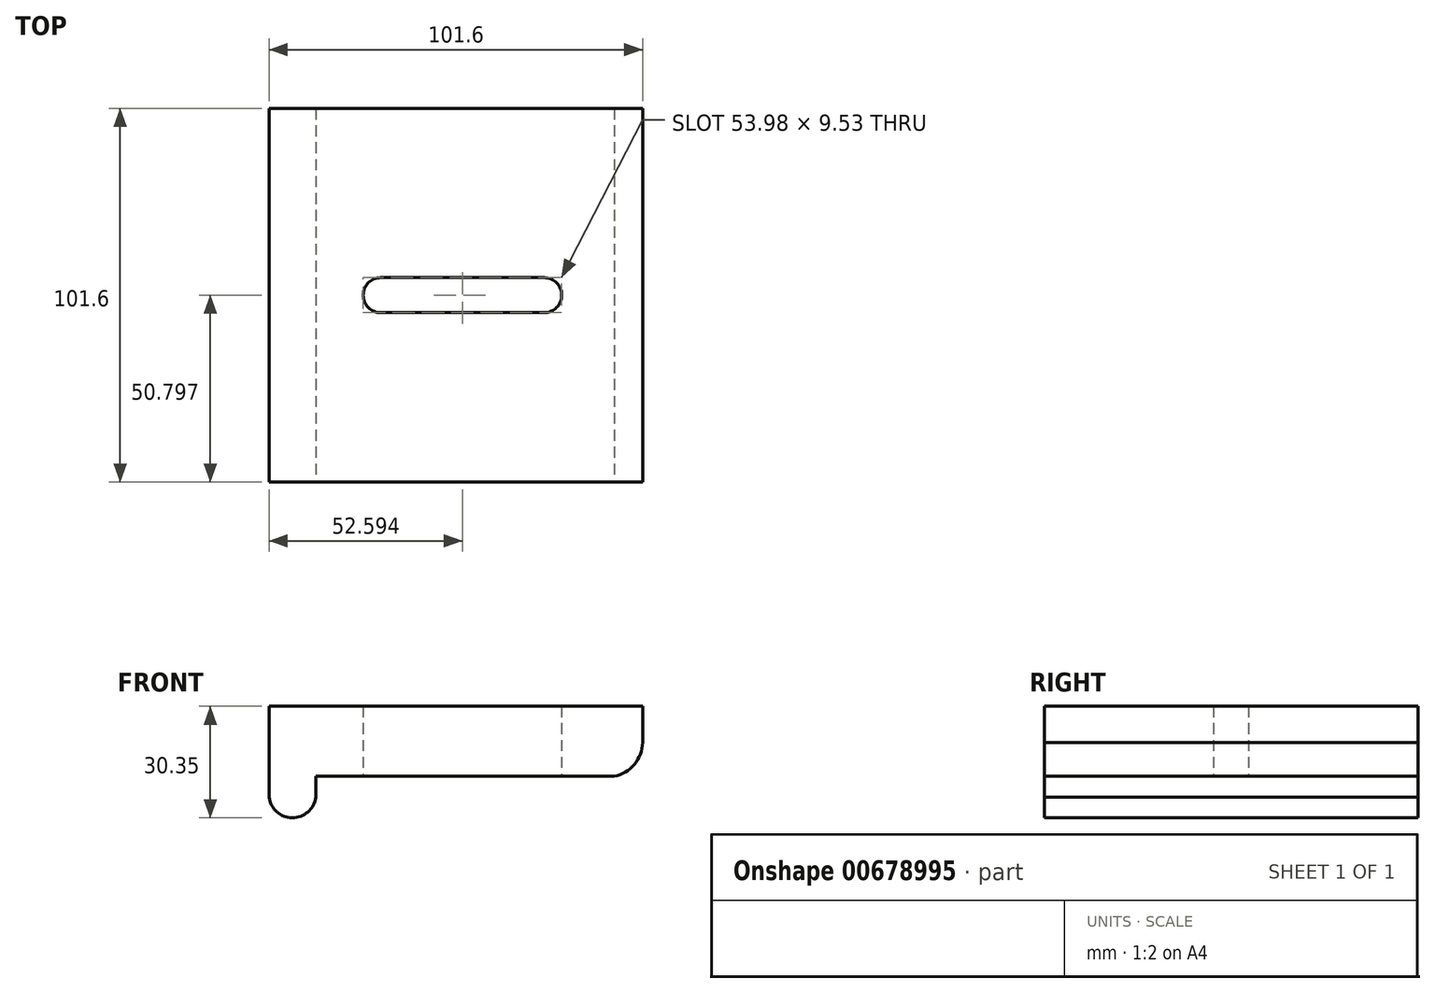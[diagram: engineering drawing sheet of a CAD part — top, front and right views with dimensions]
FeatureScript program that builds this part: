
annotation { "Feature Type Name" : "Feature", "Feature Type Description" : "" }
export const myFeature = defineFeature(function(context is Context, id is Id, definition is map)
    precondition{}
    {
        {
            var Q0;
            Q0=qCreatedBy(makeId("Top.planeOp"),FACE);
            var sketch = newSketch(context, id + "F0", { "sketchPlane" : qUnion([Q0])});
            skLineSegment(sketch, "E0", {"start": v(-101.34, 65.1) * mm, "end": v(-101.34, -36.5) * mm});
            skLineSegment(sketch, "E1", {"start": v(-101.34, -36.5) * mm, "end": v(0.26, -36.5) * mm});
            skLineSegment(sketch, "E2", {"start": v(0.26, -36.5) * mm, "end": v(0.26, 65.1) * mm});
            skLineSegment(sketch, "E3", {"start": v(0.26, 65.1) * mm, "end": v(-101.34, 65.1) * mm});
            skLineSegment(sketch, "E4", {"start": v(-70.97, 19.06) * mm, "end": v(-26.52, 19.06) * mm});
            skLineSegment(sketch, "E5", {"start": v(-26.52, 9.53) * mm, "end": v(-70.97, 9.53) * mm});
            skArc(sketch, "E6", {"start": v(-70.97, 19.06) * mm, "mid": v(-75.73, 14.3) * mm, "end": v(-70.97, 9.53) * mm});
            skArc(sketch, "E7", {"start": v(-26.52, 9.53) * mm, "mid": v(-21.76, 14.3) * mm, "end": v(-26.52, 19.06) * mm});
            skSolve(sketch);
        }
        {
            var Q0;
            Q0=makeQuery(id+"F0.imprint","IMPRINT",FACE,{"disambiguationData":[TD([[makeQuery(id+"F0.imprint","IMPRINT",EDGE,{"derivedFrom":sQuery(id+"F0.wireOp",EDGE,"E0")}),1.0]])]});
            extrude(context, id + "F1", {"entities" : qUnion([Q0]), "depth" : 19.05 * mm, "offsetDistance" : 25.4 * mm});
        }
        {
            var Q0;
            Q0=makeQuery(id+"F1.opExtrude","CAP_FACE",FACE,{"disambiguationData":[OSD([sQuery(id+"F0.wireOp",EDGE,"E0"),sQuery(id+"F0.wireOp",EDGE,"E1"),sQuery(id+"F0.wireOp",EDGE,"E2"),sQuery(id+"F0.wireOp",EDGE,"E3"),sQuery(id+"F0.wireOp",EDGE,"Ij3rbQGt-BVGS-ioUD-AomL-MFlx47e1YY0t"),sQuery(id+"F0.wireOp",EDGE,"aBqQIJp2-9Vz4-WAzg-CIwR-ENS8aY7m6kvm"),sQuery(id+"F0.wireOp",EDGE,"GVWyxK8m-kxVj-zn9I-h0XC-9meEKtxfJ6VL"),sQuery(id+"F0.wireOp",EDGE,"L1X6rBFq-LiUv-O578-zhp6-4baICqBOAP0Y")])],"isStart":true});
            var sketch = newSketch(context, id + "F2", { "sketchPlane" : qUnion([Q0])});
            skLineSegment(sketch, "E8", {"start": v(-88.64, -65.1) * mm, "end": v(-88.64, 36.5) * mm});
            skSolve(sketch);
        }
        {
            var Q0;
            Q0 = qSketchRegion(id + "F2", true);
            var Q1;
            {var subQ0=sQuery(id+"F2.wireOp",EDGE,"E8");Q1=makeQuery(id+"F2.imprint","IMPRINT",FACE,{"disambiguationData":[TD([[makeQuery(id+"F2.imprint","IMPRINT",EDGE,{"derivedFrom":subQ0}),1.0]])]});}
            extrude(context, id + "F3", {"entities" : qUnion([Q0, Q1]), "operationType" : NewBodyOperationType.ADD, "depth" : 11.43 * mm, "offsetDistance" : 25.4 * mm});
        }
        {
            var Q0;
            {var subQ0=sQuery(id+"F0.wireOp",EDGE,"E1");Q0=makeQuery(id+"F3.boolean.opBoolean","MERGE",FACE,{"derivedFrom":[makeQuery(id+"F1.opExtrude","SWEPT_FACE",FACE,{"disambiguationData":[OSD([subQ0])]}),makeQuery(id+"F3.opExtrude","SWEPT_FACE",FACE,{"disambiguationData":[OSD([subQ0])]})]});}
            var sketch = newSketch(context, id + "F4", { "sketchPlane" : qUnion([Q0])});
            skArc(sketch, "E9", {"start": v(-7.5, 0) * mm, "mid": v(-1.89, 3.35) * mm, "end": v(0.26, 9.53) * mm});
            skArc(sketch, "E10", {"start": v(-101.34, -5.69) * mm, "mid": v(-95, -11.3) * mm, "end": v(-88.64, -5.72) * mm});
            skSolve(sketch);
        }
        {
            var Q0;
            {var subQ0=sQuery(id+"F4.wireOp",EDGE,"E9");var subQ1=sQuery(id+"F0.wireOp",EDGE,"E1");var subQ2=makeQuery(id+"F1.opExtrude","CAP_EDGE",EDGE,{"disambiguationData":[OSD([subQ1])],"isStart":true});var subQ3=makeQuery(id+"F4.imprint","INTERSECT",VERTEX,{"derivedFrom":[subQ2,subQ0]});Q0=makeQuery(id+"F4.imprint","IMPRINT",FACE,{"disambiguationData":[TD([[makeQuery(id+"F4.imprint","IMPRINT",EDGE,{"disambiguationData":[TD([[subQ3,-1.0]])],"derivedFrom":subQ0}),-1.0]])]});}
            extrude(context, id + "F5", {"entities" : qUnion([Q0]), "operationType" : NewBodyOperationType.REMOVE, "endBound" : BoundingType.THROUGH_ALL, "oppositeDirection" : true, "depth" : 25.4 * mm, "offsetDistance" : 25.4 * mm});
        }
        {
            var Q0;
            {var subQ0=sQuery(id+"F4.wireOp",EDGE,"E10");Q0=makeQuery(id+"F4.imprint","IMPRINT",FACE,{"disambiguationData":[TD([[makeQuery(id+"F4.imprint","IMPRINT",EDGE,{"derivedFrom":subQ0}),-1.0]])]});}
            extrude(context, id + "F6", {"entities" : qUnion([Q0]), "operationType" : NewBodyOperationType.REMOVE, "endBound" : BoundingType.THROUGH_ALL, "oppositeDirection" : true, "depth" : 25.4 * mm, "offsetDistance" : 25.4 * mm});
        }
    });
